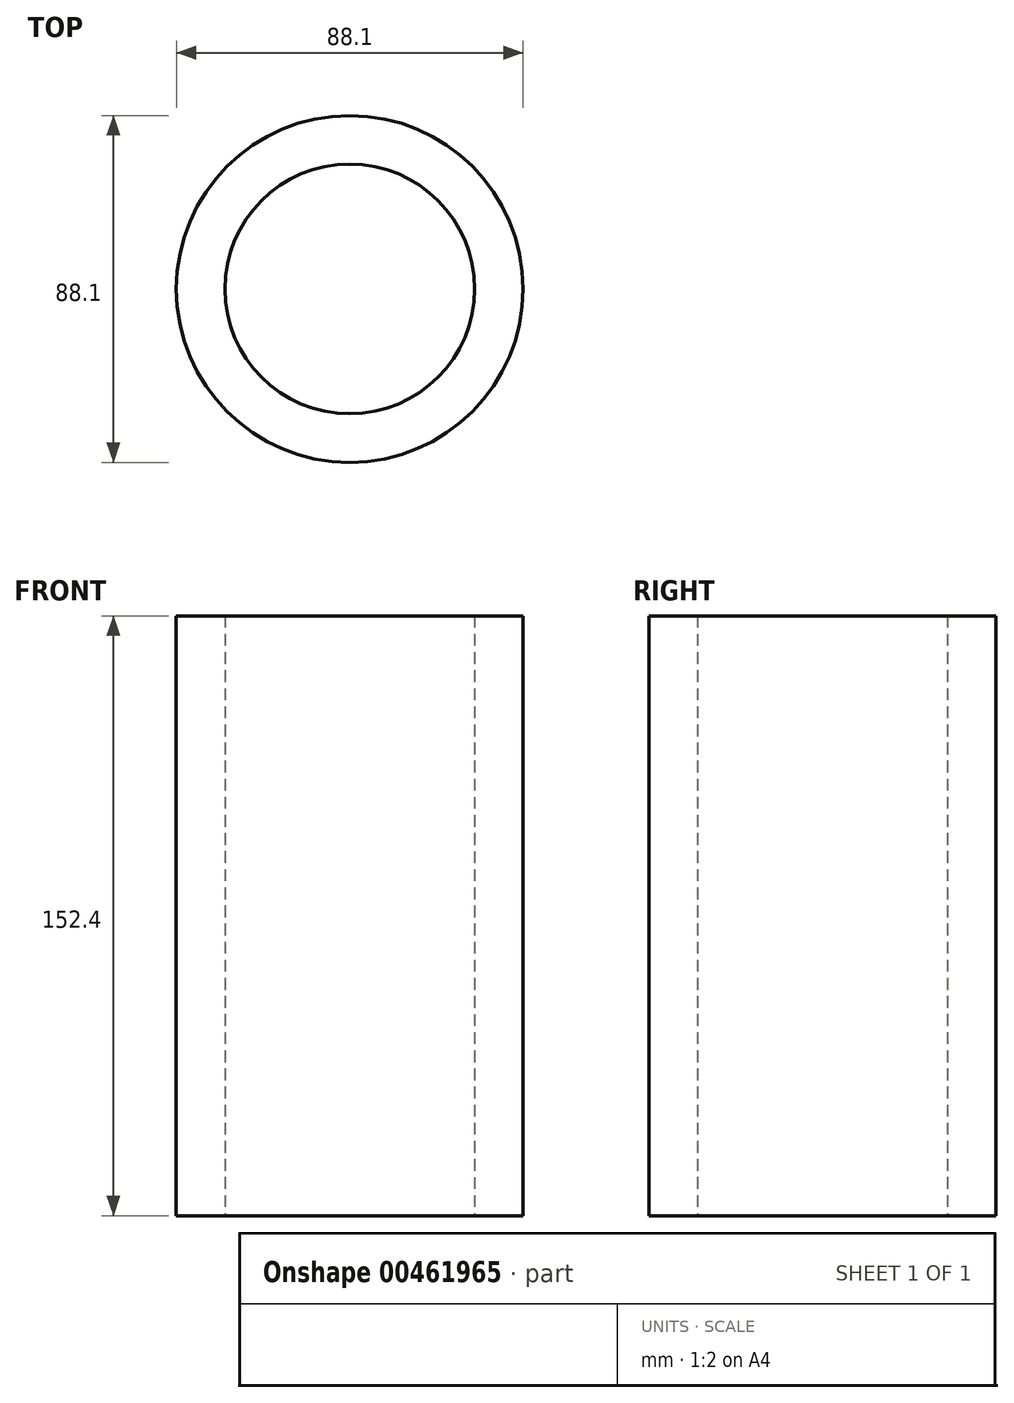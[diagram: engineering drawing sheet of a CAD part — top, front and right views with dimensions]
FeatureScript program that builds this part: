
annotation { "Feature Type Name" : "Feature", "Feature Type Description" : "" }
export const myFeature = defineFeature(function(context is Context, id is Id, definition is map)
    precondition{}
    {
        {
            var Q0;
            Q0=qCreatedBy(makeId("Top.planeOp"),FACE);
            var sketch = newSketch(context, id + "F0", { "sketchPlane" : qUnion([Q0])});
            skCircle(sketch, "E0", {"center": v(0, 0) * mm, "radius": 44.05 * mm});
            skCircle(sketch, "E1", {"center": v(0, 0) * mm, "radius": 31.73 * mm});
            skSolve(sketch);
        }
        {
            var Q0;
            Q0 = qSketchRegion(id + "F0", true);
            var Q1;
            Q1=makeQuery(id+"F0.imprint","IMPRINT",FACE,{"disambiguationData":[TD([[makeQuery(id+"F0.imprint","IMPRINT",EDGE,{"derivedFrom":sQuery(id+"F0.wireOp",EDGE,"E0")}),1.0]])]});
            extrude(context, id + "F1", {"entities" : qUnion([Q0, Q1]), "depth" : 152.4 * mm});
        }
    });
